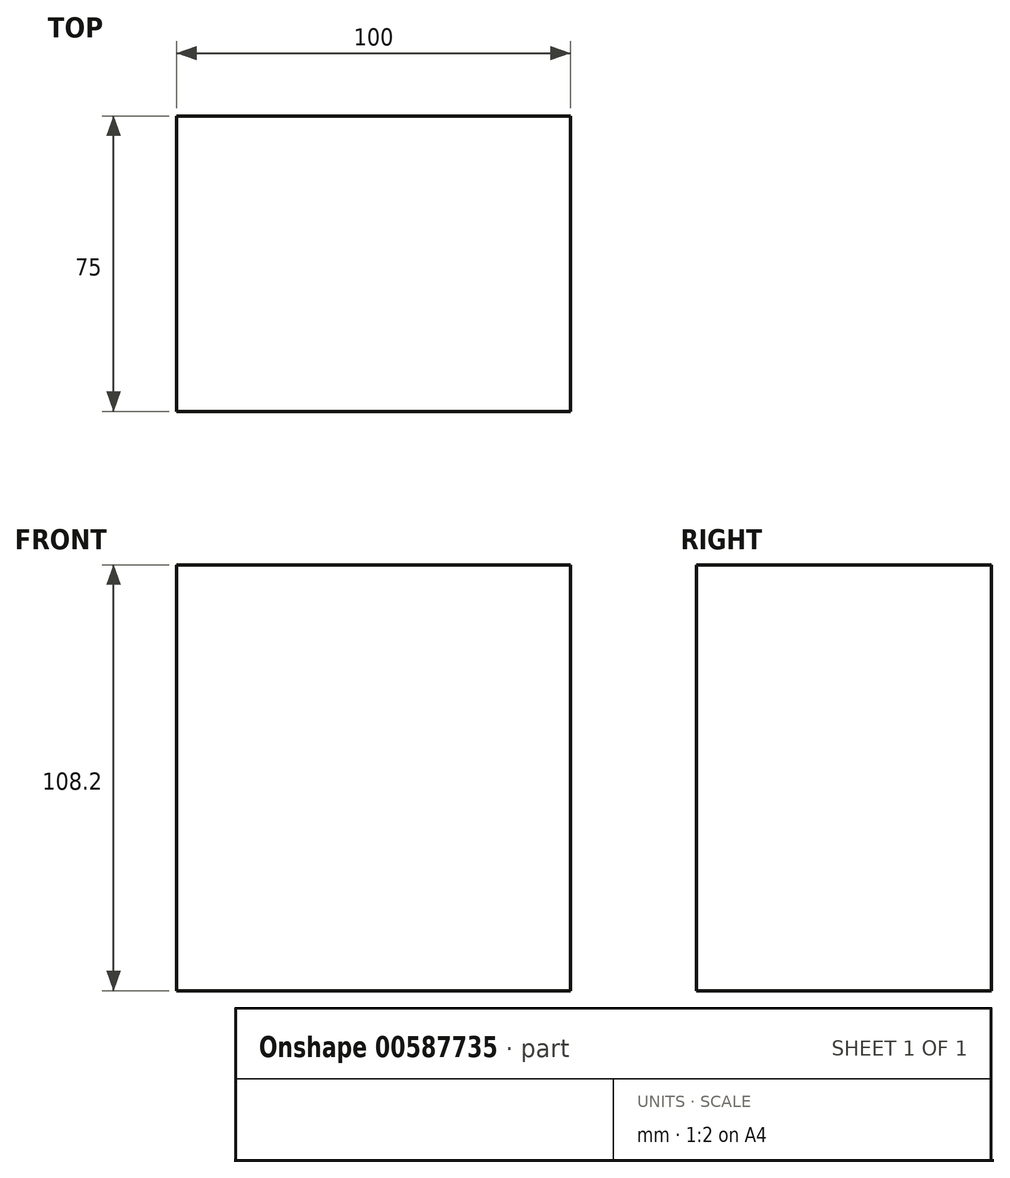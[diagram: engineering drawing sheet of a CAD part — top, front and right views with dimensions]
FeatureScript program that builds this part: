
annotation { "Feature Type Name" : "Feature", "Feature Type Description" : "" }
export const myFeature = defineFeature(function(context is Context, id is Id, definition is map)
    precondition{}
    {
        {
            var Q0;
            Q0=qCreatedBy(makeId("Top.planeOp"),FACE);
            var sketch = newSketch(context, id + "F0", { "sketchPlane" : qUnion([Q0])});
            skLineSegment(sketch, "E0.bottom", {"start": v(-54.44, 40.9) * mm, "end": v(45.56, 40.9) * mm});
            skLineSegment(sketch, "E0.top", {"start": v(-54.44, -34.1) * mm, "end": v(45.56, -34.1) * mm});
            skLineSegment(sketch, "E0.left", {"start": v(-54.44, 40.9) * mm, "end": v(-54.44, -34.1) * mm});
            skLineSegment(sketch, "E0.right", {"start": v(45.56, 40.9) * mm, "end": v(45.56, -34.1) * mm});
            skSolve(sketch);
        }
        {
            var Q0;
            Q0=makeQuery(id+"F0.imprint","IMPRINT",FACE,{"disambiguationData":[TD([[makeQuery(id+"F0.imprint","IMPRINT",EDGE,{"derivedFrom":sQuery(id+"F0.wireOp",EDGE,"E0.bottom")}),-1.0]])]});
            extrude(context, id + "F1", {"entities" : qUnion([Q0]), "depth" : 108.2 * mm, "offsetDistance" : 25 * mm});
        }
    });
